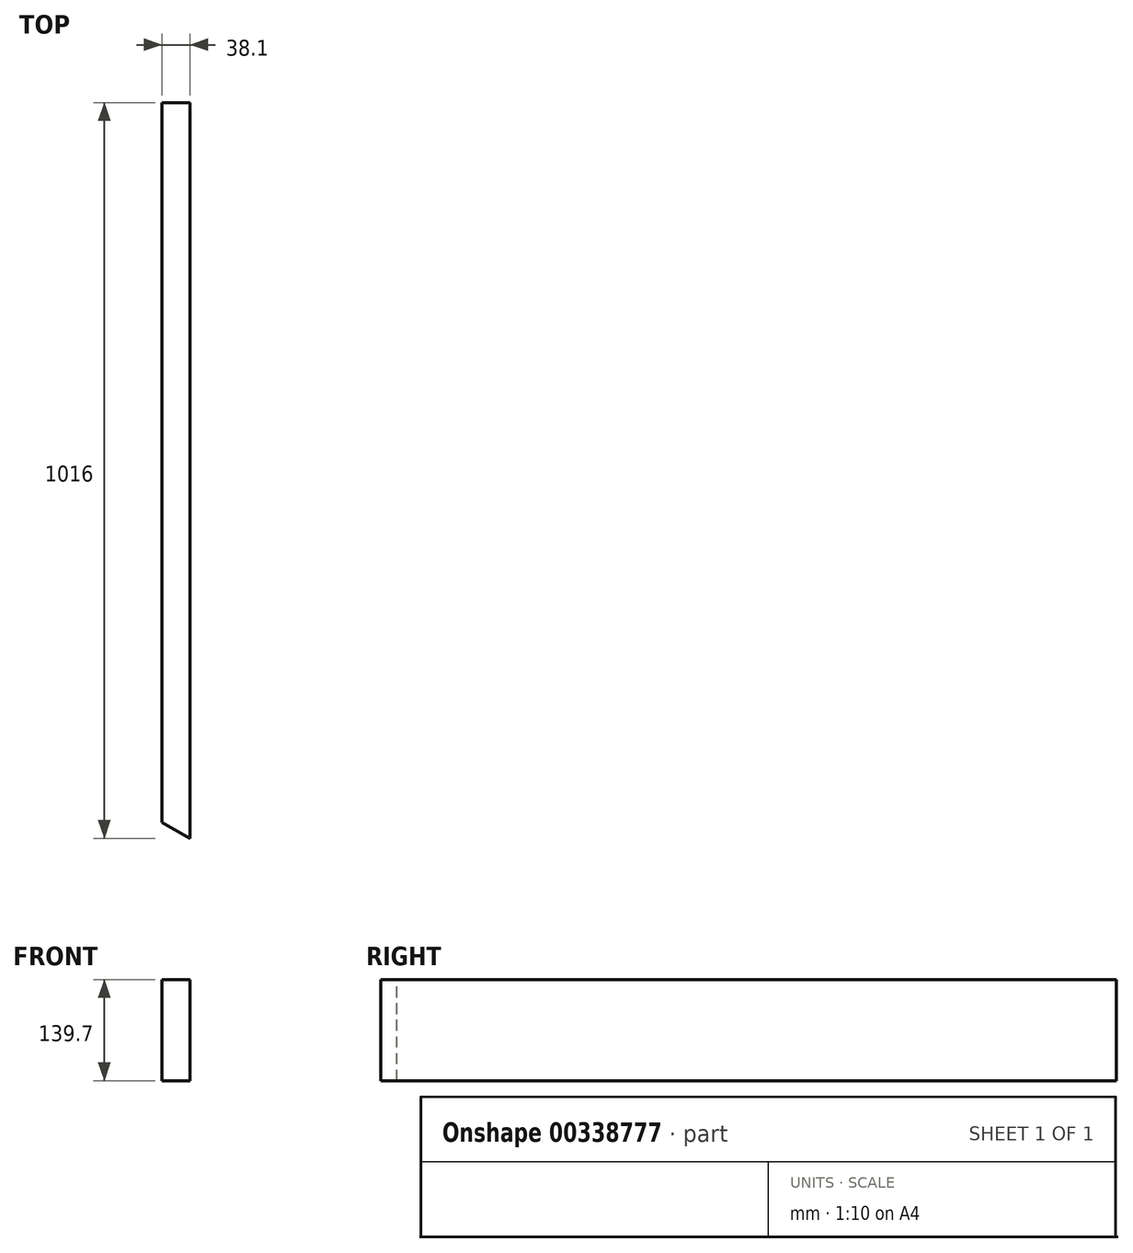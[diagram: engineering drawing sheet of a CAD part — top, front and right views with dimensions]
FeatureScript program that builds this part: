
annotation { "Feature Type Name" : "Feature", "Feature Type Description" : "" }
export const myFeature = defineFeature(function(context is Context, id is Id, definition is map)
    precondition{}
    {
        {
            var Q0;
            Q0=qCreatedBy(makeId("Front.planeOp"),FACE);
            var sketch = newSketch(context, id + "F0", { "sketchPlane" : qUnion([Q0])});
            skLineSegment(sketch, "E0.bottom", {"start": v(0, 0) * mm, "end": v(-38.1, 0) * mm});
            skLineSegment(sketch, "E0.top", {"start": v(0, 88.9) * mm, "end": v(-38.1, 88.9) * mm});
            skLineSegment(sketch, "E0.left", {"start": v(0, 0) * mm, "end": v(0, 88.9) * mm});
            skLineSegment(sketch, "E0.right", {"start": v(-38.1, 0) * mm, "end": v(-38.1, 88.9) * mm});
            skSolve(sketch);
        }
        {
            var Q0;
            Q0=makeQuery(id+"F0.imprint","IMPRINT",FACE,{"disambiguationData":[TD([[makeQuery(id+"F0.imprint","IMPRINT",EDGE,{"derivedFrom":sQuery(id+"F0.wireOp",EDGE,"E0.bottom")}),-1.0]])]});
            extrude(context, id + "F1", {"entities" : qUnion([Q0]), "depth" : 1016 * mm});
        }
        {
            var Q0;
            Q0=makeQuery(id+"F1.opExtrude","SWEPT_BODY",BODY,{"disambiguationData":[OSD([sQuery(id+"F0.wireOp",EDGE,"E0.bottom"),sQuery(id+"F0.wireOp",EDGE,"E0.top"),sQuery(id+"F0.wireOp",EDGE,"E0.left"),sQuery(id+"F0.wireOp",EDGE,"E0.right")])]});
            transform(context, id + "F2", {"entities" : qUnion([Q0]), "transformType" : TransformType.TRANSLATION_3D, "dx" : 76.2 * mm, "dy" : 0 * mm, "dz" : 0 * mm, "makeCopy" : true});
        }
        {
            var Q0;
            Q0=makeQuery(id+"F1.opExtrude","SWEPT_FACE",FACE,{"disambiguationData":[OSD([sQuery(id+"F0.wireOp",EDGE,"E0.top")])]});
            var sketch = newSketch(context, id + "F3", { "sketchPlane" : qUnion([Q0])});
            skLineSegment(sketch, "E1", {"start": v(0, -1016) * mm, "end": v(-38.1, -994) * mm});
            skSolve(sketch);
        }
        {
            var Q0;
            {var subQ0=sQuery(id+"F3.wireOp",EDGE,"E1");Q0=makeQuery(id+"F3.imprint","IMPRINT",FACE,{"disambiguationData":[TD([[makeQuery(id+"F3.imprint","IMPRINT",EDGE,{"derivedFrom":subQ0}),1.0]])]});}
            extrude(context, id + "F4", {"entities" : qUnion([Q0]), "operationType" : NewBodyOperationType.REMOVE, "oppositeDirection" : true, "depth" : 88.9 * mm});
        }
        {
            var Q0;
            Q0=makeQuery(id+"F1.opExtrude","SWEPT_FACE",FACE,{"disambiguationData":[OSD([sQuery(id+"F0.wireOp",EDGE,"E0.top")])]});
            extrude(context, id + "F5", {"entities" : qUnion([Q0]), "operationType" : NewBodyOperationType.ADD, "depth" : 50.8 * mm});
        }
        {
            var Q0;
            Q0=makeQuery(id+"F2.opPattern","COPY",BODY,{"derivedFrom":makeQuery(id+"F1.opExtrude","SWEPT_BODY",BODY,{"disambiguationData":[OSD([sQuery(id+"F0.wireOp",EDGE,"E0.bottom"),sQuery(id+"F0.wireOp",EDGE,"E0.top"),sQuery(id+"F0.wireOp",EDGE,"E0.left"),sQuery(id+"F0.wireOp",EDGE,"E0.right")])]}),"instanceName":"1"});
            deleteBodies(context, id + "F6", {"entities" : qUnion([Q0])});
        }
    });
